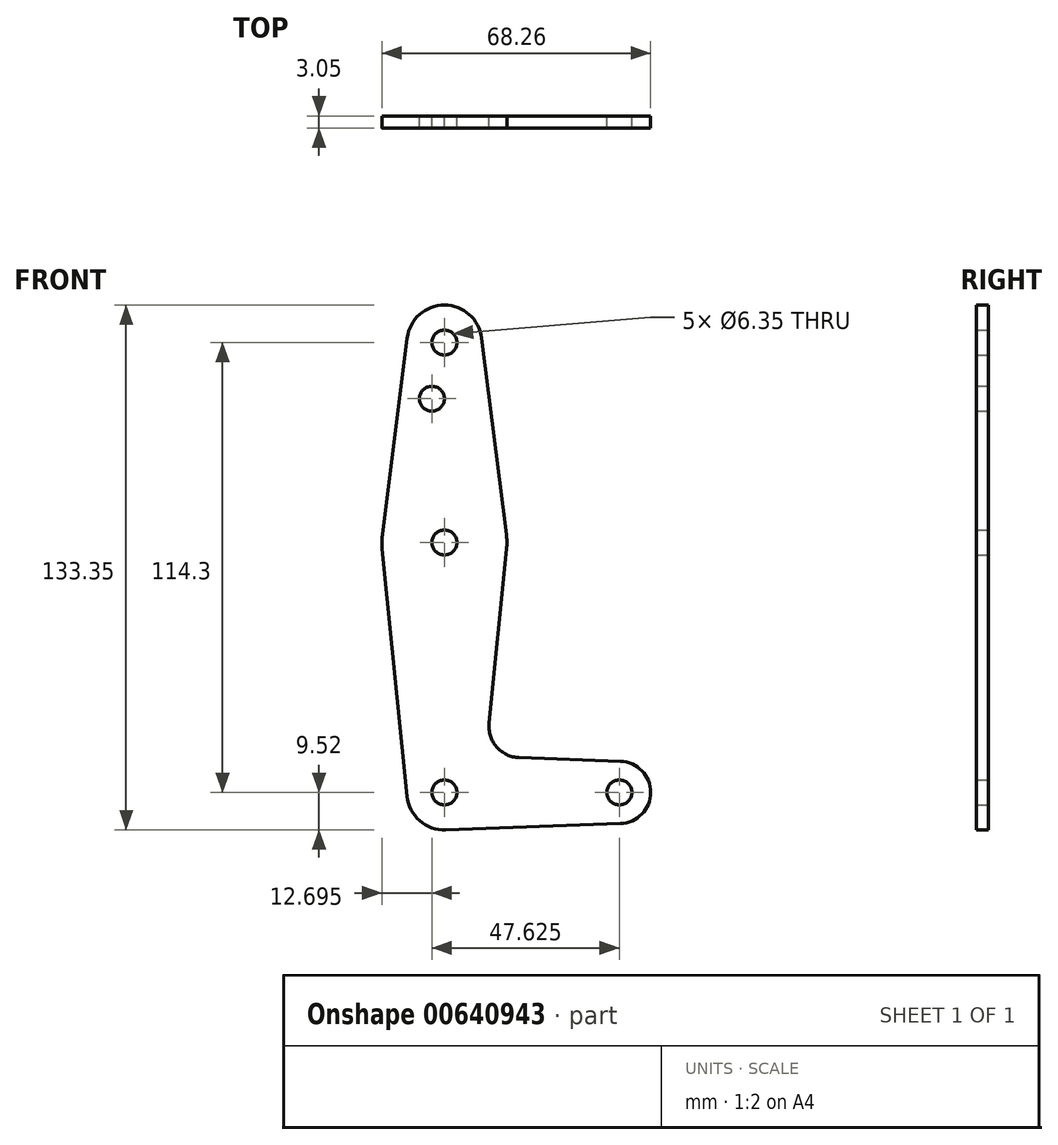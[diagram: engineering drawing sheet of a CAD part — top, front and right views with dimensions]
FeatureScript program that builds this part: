
annotation { "Feature Type Name" : "Feature", "Feature Type Description" : "" }
export const myFeature = defineFeature(function(context is Context, id is Id, definition is map)
    precondition{}
    {
        {
            var Q0;
            Q0=qCreatedBy(makeId("Front.planeOp"),FACE);
            var sketch = newSketch(context, id + "F0", { "sketchPlane" : qUnion([Q0])});
            skLineSegment(sketch, "E0", {"start": v(0, 0) * mm, "end": v(0, 114.3) * mm, "construction": true});
            skLineSegment(sketch, "E1", {"start": v(0, 0) * mm, "end": v(44.45, 0) * mm});
            skCircle(sketch, "E2", {"center": v(0, 114.3) * mm, "radius": 9.53 * mm});
            skLineSegment(sketch, "E3", {"start": v(0, 0) * mm, "end": v(0, 63.5) * mm, "construction": true});
            skCircle(sketch, "E4", {"center": v(0, 63.5) * mm, "radius": 15.88 * mm});
            skCircle(sketch, "E5", {"center": v(0, 0) * mm, "radius": 9.53 * mm});
            skCircle(sketch, "E6", {"center": v(44.45, 0) * mm, "radius": 7.94 * mm});
            skLineSegment(sketch, "E7", {"start": v(18.97, 8.85) * mm, "end": v(44.73, 7.93) * mm});
            skLineSegment(sketch, "E8", {"start": v(0.34, -9.52) * mm, "end": v(44.73, -7.93) * mm});
            skLineSegment(sketch, "E9", {"start": v(-9.48, -0.95) * mm, "end": v(-15.8, 61.91) * mm});
            skLineSegment(sketch, "E10", {"start": v(-15.75, 65.48) * mm, "end": v(-9.45, 115.5) * mm});
            skLineSegment(sketch, "E11", {"start": v(9.45, 115.5) * mm, "end": v(15.75, 65.48) * mm});
            skLineSegment(sketch, "E12", {"start": v(15.8, 61.91) * mm, "end": v(11.34, 17.6) * mm});
            skArc(sketch, "E13.filletArc", {"start": v(11.34, 17.6) * mm, "mid": v(13.26, 11.57) * mm, "end": v(18.97, 8.85) * mm});
            skCircle(sketch, "E14", {"center": v(0, 114.3) * mm, "radius": 3.18 * mm});
            skCircle(sketch, "E15", {"center": v(0, 63.5) * mm, "radius": 3.18 * mm});
            skCircle(sketch, "E16", {"center": v(0, 0) * mm, "radius": 3.18 * mm});
            skCircle(sketch, "E17", {"center": v(44.45, 0) * mm, "radius": 3.18 * mm});
            skCircle(sketch, "E18", {"center": v(-3.18, 100.03) * mm, "radius": 3.18 * mm});
            skSolve(sketch);
        }
        {
            var Q0;
            Q0 = qSketchRegion(id + "F0", true);
            extrude(context, id + "F1", {"entities" : qUnion([Q0]), "depth" : 3.05 * mm, "offsetDistance" : 25.4 * mm});
        }
    });
